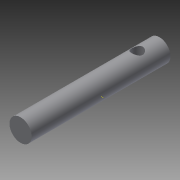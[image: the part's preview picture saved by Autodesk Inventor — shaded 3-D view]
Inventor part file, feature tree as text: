
AUTODESK INVENTOR PART (.ipt)
format: ipt  version: 2015 SP1 (Build 190203100, 203)  size: 86,016 bytes
history: native  units: in
note: dims shown in document units (in); Inventor stores cm internally (conversion verified against a paired STEP export)
features: sketch x2, extrude x1, plane x1, hole x1
ambient origin geometry x8: Origin, YZ Plane, XZ Plane, XY Plane, X Axis, Y Axis, Z Axis, Center Point
bodies: Body1 (feature_tree)
feature tree (5):
  extrude  "Extrusion5"  Depth=1.9685in TaperAngle=0.0deg
  plane  "Work Plane1"
  hole  "Hole1"  [1 undecoded]
  sketch  "Sketch5"  dims[d17=0.315in d18=1.9685in d19=0.0in]
  sketch  "Sketch7"  dims[d25=0.315in d26=0.1276in d27=0.315in d28=0.1575in d29=0.0787in d30=90.0deg d31=0.4646in d32=0.8108in d33=0.1575in]
note: 1 required parameter value undecoded (feature->parameter linkage not recoverable at this tier; creation-order binding heuristic only, values carry confidence <= 0.55)
